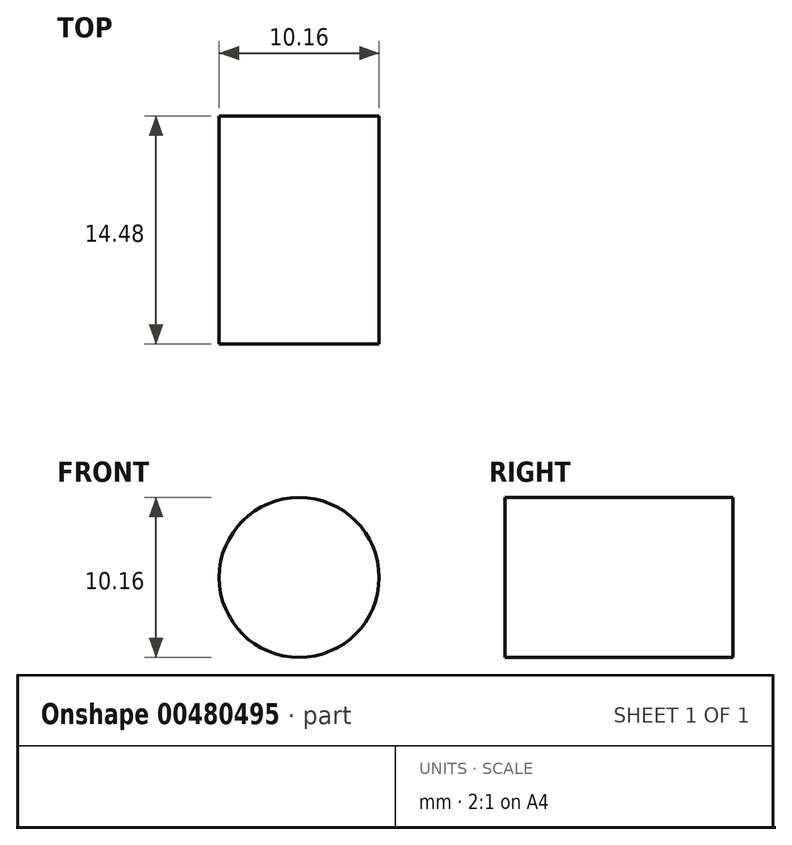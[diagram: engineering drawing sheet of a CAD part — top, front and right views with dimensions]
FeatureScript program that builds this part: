
annotation { "Feature Type Name" : "Feature", "Feature Type Description" : "" }
export const myFeature = defineFeature(function(context is Context, id is Id, definition is map)
    precondition{}
    {
        {
            var Q0;
            Q0=qCreatedBy(makeId("Front.planeOp"),FACE);
            var sketch = newSketch(context, id + "F0", { "sketchPlane" : qUnion([Q0])});
            skCircle(sketch, "E0", {"center": v(0, 0) * mm, "radius": 5.08 * mm});
            skSolve(sketch);
        }
        {
            var Q0;
            Q0 = qSketchRegion(id + "F0", true);
            var Q1;
            Q1=makeQuery(id+"F0.imprint","IMPRINT",FACE,{"disambiguationData":[TD([[makeQuery(id+"F0.imprint","IMPRINT",EDGE,{"derivedFrom":sQuery(id+"F0.wireOp",EDGE,"E0")}),1.0]])]});
            extrude(context, id + "F1", {"entities" : qUnion([Q0, Q1]), "depth" : 14.48 * mm});
        }
    });
